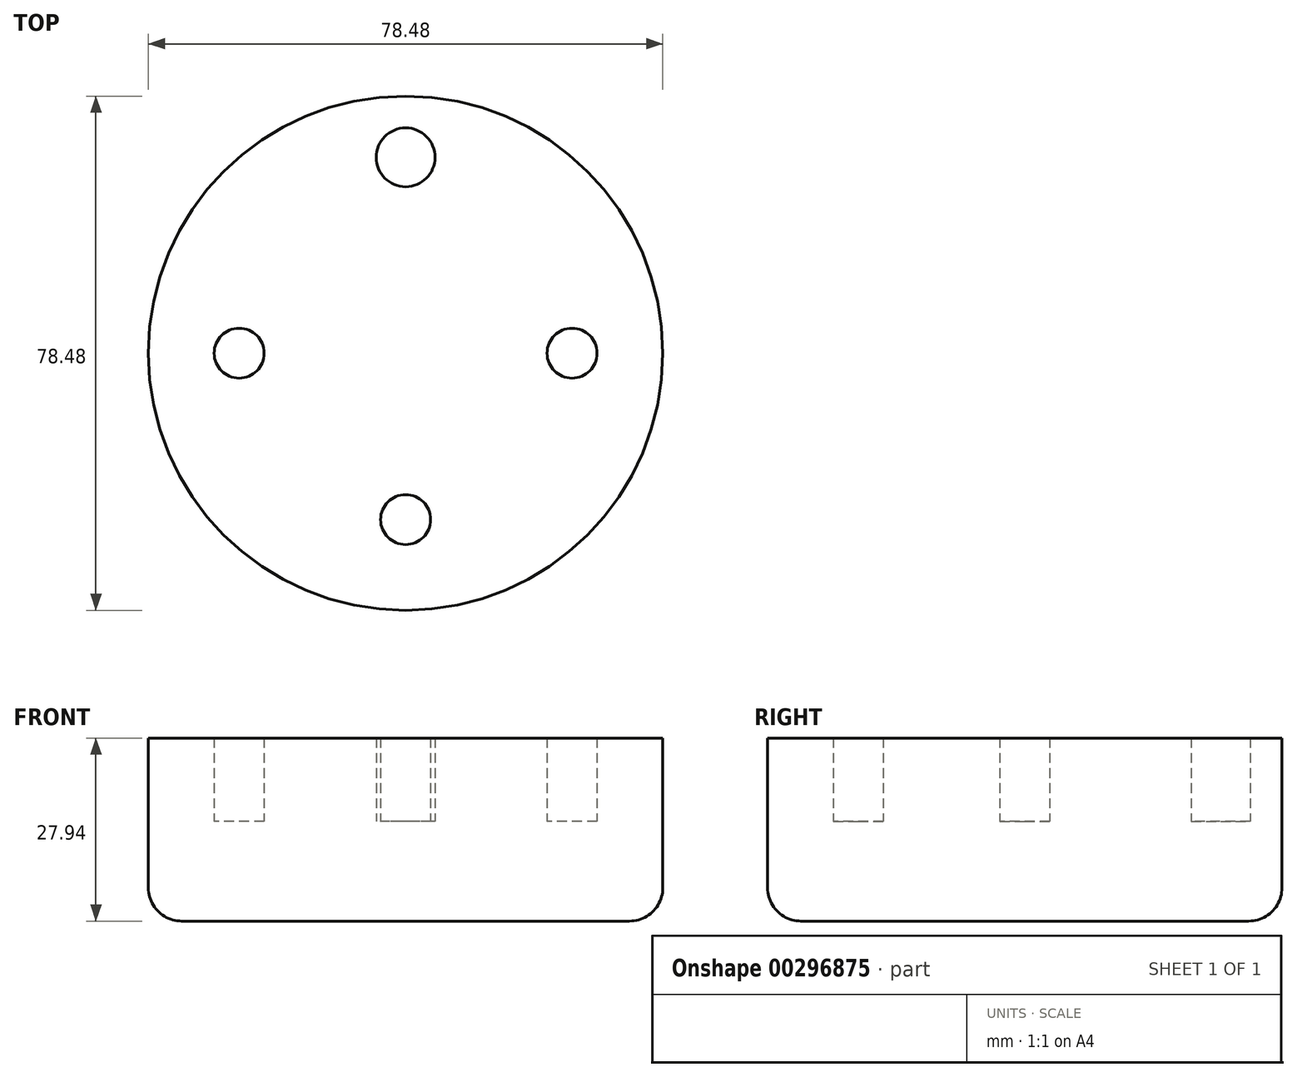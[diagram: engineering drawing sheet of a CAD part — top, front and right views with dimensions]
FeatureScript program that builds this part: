
annotation { "Feature Type Name" : "Feature", "Feature Type Description" : "" }
export const myFeature = defineFeature(function(context is Context, id is Id, definition is map)
    precondition{}
    {
        {
            var Q0;
            Q0=qCreatedBy(makeId("Top.planeOp"),FACE);
            var sketch = newSketch(context, id + "F0", { "sketchPlane" : qUnion([Q0])});
            skCircle(sketch, "E0", {"center": v(0, 0) * mm, "radius": 39.24 * mm});
            skSolve(sketch);
        }
        {
            var Q0;
            Q0=makeQuery(id+"F0.imprint","IMPRINT",FACE,{"disambiguationData":[TD([[makeQuery(id+"F0.imprint","IMPRINT",EDGE,{"derivedFrom":sQuery(id+"F0.wireOp",EDGE,"E0")}),1.0]])]});
            extrude(context, id + "F1", {"entities" : qUnion([Q0]), "depth" : 15.24 * mm});
        }
        {
            var Q0;
            Q0=makeQuery(id+"F1.opExtrude","CAP_FACE",FACE,{"disambiguationData":[OSD([sQuery(id+"F0.wireOp",EDGE,"E0")])],"isStart":false});
            var sketch = newSketch(context, id + "F2", { "sketchPlane" : qUnion([Q0])});
            skCircle(sketch, "E1", {"center": v(0, -25.4) * mm, "radius": 3.81 * mm});
            skCircle(sketch, "E2", {"center": v(0, 29.9) * mm, "radius": 4.5 * mm});
            skSolve(sketch);
        }
        {
            var Q0;
            Q0=makeQuery(id+"F2.imprint","IMPRINT",FACE,{"disambiguationData":[TD([[makeQuery(id+"F2.imprint","IMPRINT",EDGE,{"derivedFrom":sQuery(id+"F2.wireOp",EDGE,"E1")}),-1.0]])]});
            var sketch = newSketch(context, id + "F3", { "sketchPlane" : qUnion([Q0])});
            skCircle(sketch, "E3", {"center": v(-25.4, 0) * mm, "radius": 3.81 * mm});
            skCircle(sketch, "E4", {"center": v(25.4, 0) * mm, "radius": 3.81 * mm});
            skSolve(sketch);
        }
        {
            var Q0;
            Q0=makeQuery(id+"F3.imprint","IMPRINT",FACE,{"disambiguationData":[TD([[makeQuery(id+"F3.imprint","IMPRINT",EDGE,{"derivedFrom":sQuery(id+"F3.wireOp",EDGE,"E3")}),-1.0]])]});
            var Q1;
            Q1=sQuery(id+"F3.wireOp",EDGE,"E3");
            var Q2;
            Q2=sQuery(id+"F2.wireOp",EDGE,"E2");
            var Q3;
            Q3=sQuery(id+"F3.wireOp",EDGE,"E4");
            var Q4;
            Q4=sQuery(id+"F2.wireOp",EDGE,"E1");
            extrude(context, id + "F4", {"entities" : qUnion([Q0]), "operationType" : NewBodyOperationType.ADD, "surfaceEntities" : qUnion([Q1, Q2, Q3, Q4]), "depth" : 12.7 * mm});
        }
        {
            var Q0;
            Q0=makeQuery(id+"F1.opExtrude","CAP_EDGE",EDGE,{"disambiguationData":[OSD([sQuery(id+"F0.wireOp",EDGE,"E0")])],"isStart":true});
            fillet(context, id + "F5", {"entities" : qUnion([Q0]), "radius" : 5.08 * mm, "tangentPropagation" : true, "allowEdgeOverflow" : false});
        }
    });
